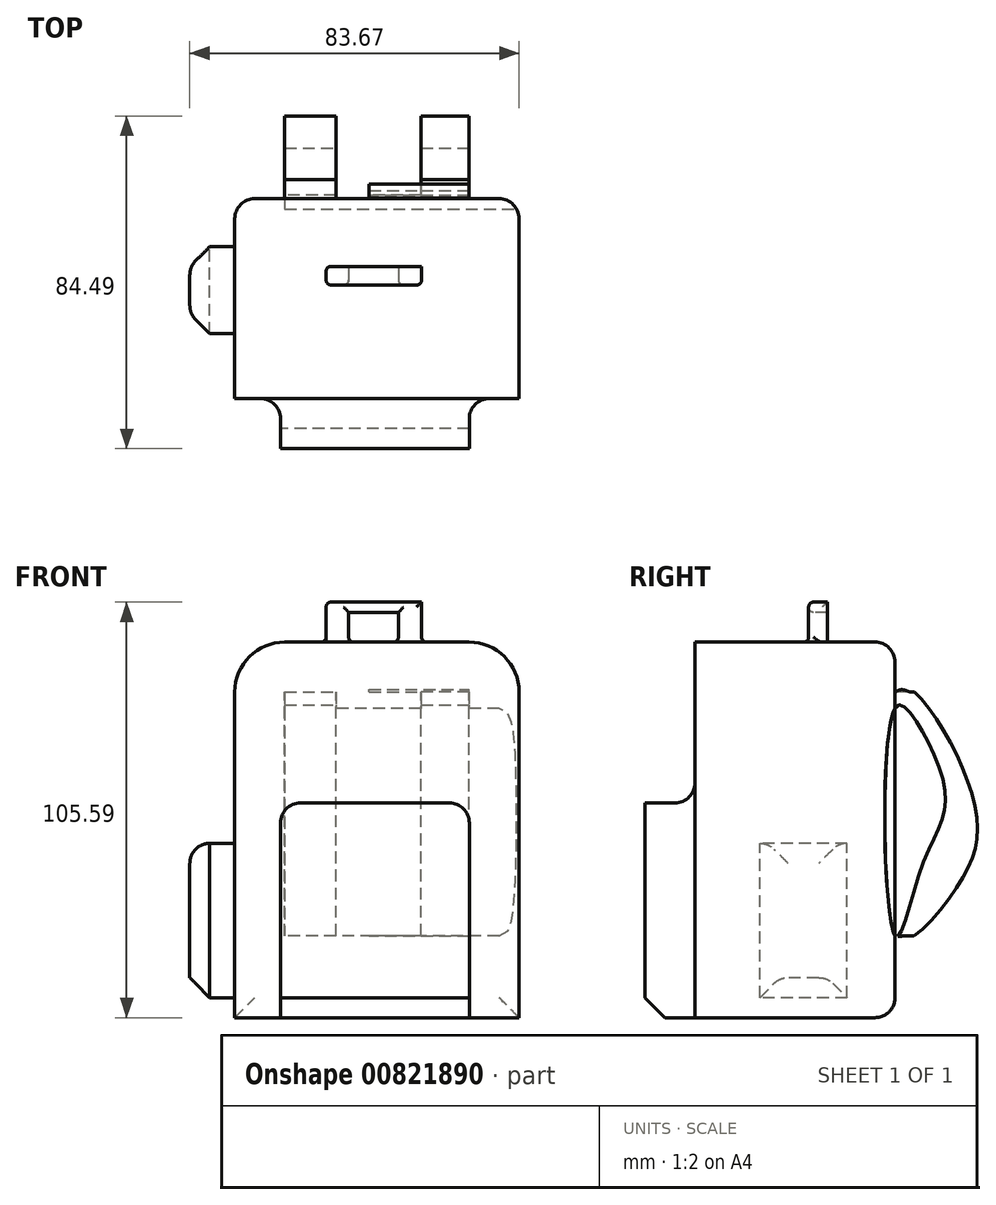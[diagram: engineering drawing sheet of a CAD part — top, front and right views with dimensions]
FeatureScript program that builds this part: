
annotation { "Feature Type Name" : "Feature", "Feature Type Description" : "" }
export const myFeature = defineFeature(function(context is Context, id is Id, definition is map)
    precondition{}
    {
        {
            var Q0;
            Q0=qCreatedBy(makeId("Front.planeOp"),FACE);
            var sketch = newSketch(context, id + "F0", { "sketchPlane" : qUnion([Q0])});
            skLineSegment(sketch, "E0.bottom", {"start": v(-29.99, 56.61) * mm, "end": v(42.25, 56.61) * mm});
            skLineSegment(sketch, "E0.top", {"start": v(-29.99, -38.82) * mm, "end": v(42.25, -38.82) * mm});
            skLineSegment(sketch, "E0.left", {"start": v(-29.99, 56.61) * mm, "end": v(-29.99, -38.82) * mm});
            skLineSegment(sketch, "E0.right", {"start": v(42.25, 56.61) * mm, "end": v(42.25, -38.82) * mm});
            skSolve(sketch);
        }
        {
            var Q0;
            Q0 = qSketchRegion(id + "F0", true);
            extrude(context, id + "F1", {"entities" : qUnion([Q0]), "depth" : 63.5 * mm, "offsetDistance" : 25.4 * mm});
        }
        {
            var Q0;
            Q0=makeQuery(id+"F1.opExtrude","CAP_FACE",FACE,{"disambiguationData":[OSD([sQuery(id+"F0.wireOp",EDGE,"E0.bottom"),sQuery(id+"F0.wireOp",EDGE,"E0.top"),sQuery(id+"F0.wireOp",EDGE,"E0.left"),sQuery(id+"F0.wireOp",EDGE,"E0.right")])],"isStart":false});
            var sketch = newSketch(context, id + "F2", { "sketchPlane" : qUnion([Q0])});
            skLineSegment(sketch, "E1.bottom", {"start": v(-18.39, -38.82) * mm, "end": v(29.6, -38.82) * mm});
            skLineSegment(sketch, "E1.top", {"start": v(-18.39, 15.75) * mm, "end": v(29.6, 15.75) * mm});
            skLineSegment(sketch, "E1.left", {"start": v(-18.39, -38.82) * mm, "end": v(-18.39, 15.75) * mm});
            skLineSegment(sketch, "E1.right", {"start": v(29.6, -38.82) * mm, "end": v(29.6, 15.75) * mm});
            skSolve(sketch);
        }
        {
            var Q0;
            Q0=makeQuery(id+"F2.imprint","IMPRINT",FACE,{"disambiguationData":[TD([[makeQuery(id+"F2.imprint","IMPRINT",EDGE,{"derivedFrom":sQuery(id+"F2.wireOp",EDGE,"E1.top")}),1.0]])]});
            extrude(context, id + "F3", {"entities" : qUnion([Q0]), "operationType" : NewBodyOperationType.REMOVE, "oppositeDirection" : true, "depth" : 12.7 * mm, "offsetDistance" : 25.4 * mm});
        }
        {
            var Q0;
            Q0=makeQuery(id+"F3.boolean.opBoolean","COPY",EDGE,{"derivedFrom":makeQuery(id+"F3.opExtrude","CAP_EDGE",EDGE,{"disambiguationData":[OSD([sQuery(id+"F2.wireOp",EDGE,"E1.left")])],"isStart":true})});
            var Q1;
            Q1=makeQuery(id+"F3.boolean.opBoolean","COPY",EDGE,{"derivedFrom":makeQuery(id+"F3.opExtrude","CAP_EDGE",EDGE,{"disambiguationData":[OSD([sQuery(id+"F2.wireOp",EDGE,"E1.top")])],"isStart":true})});
            var Q2;
            Q2=makeQuery(id+"F3.boolean.opBoolean","COPY",EDGE,{"derivedFrom":makeQuery(id+"F3.opExtrude","CAP_EDGE",EDGE,{"disambiguationData":[OSD([sQuery(id+"F2.wireOp",EDGE,"E1.top")])],"isStart":false})});
            var Q3;
            Q3=makeQuery(id+"F3.boolean.opBoolean","COPY",EDGE,{"derivedFrom":makeQuery(id+"F3.opExtrude","CAP_EDGE",EDGE,{"disambiguationData":[OSD([sQuery(id+"F2.wireOp",EDGE,"E1.left")])],"isStart":false})});
            var Q4;
            Q4=makeQuery(id+"F3.boolean.opBoolean","COPY",EDGE,{"derivedFrom":makeQuery(id+"F3.opExtrude","CAP_EDGE",EDGE,{"disambiguationData":[OSD([sQuery(id+"F2.wireOp",EDGE,"E1.right")])],"isStart":false})});
            var Q5;
            Q5=makeQuery(id+"F3.boolean.opBoolean","COPY",EDGE,{"derivedFrom":makeQuery(id+"F3.opExtrude","CAP_EDGE",EDGE,{"disambiguationData":[OSD([sQuery(id+"F2.wireOp",EDGE,"E1.right")])],"isStart":true})});
            var Q6;
            Q6=makeQuery(id+"F3.boolean.opBoolean","COPY",EDGE,{"derivedFrom":makeQuery(id+"F3.opExtrude","SWEPT_EDGE",EDGE,{"disambiguationData":[OSD([sQuery(id+"F2.wireOp",EDGE,"E1.top"),sQuery(id+"F2.wireOp",EDGE,"E1.right")])]})});
            var Q7;
            Q7=makeQuery(id+"F3.boolean.opBoolean","COPY",EDGE,{"derivedFrom":makeQuery(id+"F3.opExtrude","SWEPT_EDGE",EDGE,{"disambiguationData":[OSD([sQuery(id+"F2.wireOp",EDGE,"E1.top"),sQuery(id+"F2.wireOp",EDGE,"E1.left")])]})});
            fillet(context, id + "F4", {"entities" : qUnion([Q0, Q1, Q2, Q3, Q4, Q5, Q6, Q7]), "radius" : 5.08 * mm, "tangentPropagation" : true, "allowEdgeOverflow" : false});
        }
        {
            var Q0;
            Q0=makeQuery(id+"F3.boolean.opBoolean","COPY",EDGE,{"derivedFrom":makeQuery(id+"F3.opExtrude","CAP_EDGE",EDGE,{"disambiguationData":[OSD([sQuery(id+"F0.wireOp",EDGE,"E0.bottom")])],"isStart":false})});
            var Q1;
            Q1=makeQuery(id+"F3.boolean.opBoolean","COPY",EDGE,{"derivedFrom":makeQuery(id+"F3.opExtrude","CAP_EDGE",EDGE,{"disambiguationData":[OSD([sQuery(id+"F0.wireOp",EDGE,"E0.right")])],"isStart":false})});
            var Q2;
            Q2=makeQuery(id+"F3.boolean.opBoolean","COPY",EDGE,{"derivedFrom":makeQuery(id+"F3.opExtrude","CAP_EDGE",EDGE,{"disambiguationData":[OSD([sQuery(id+"F0.wireOp",EDGE,"E0.left")])],"isStart":false})});
            var Q3;
            Q3=makeQuery(id+"F1.opExtrude","SWEPT_EDGE",EDGE,{"disambiguationData":[OSD([sQuery(id+"F0.wireOp",EDGE,"E0.bottom"),sQuery(id+"F0.wireOp",EDGE,"E0.right")])]});
            var Q4;
            Q4=makeQuery(id+"F1.opExtrude","SWEPT_EDGE",EDGE,{"disambiguationData":[OSD([sQuery(id+"F0.wireOp",EDGE,"E0.bottom"),sQuery(id+"F0.wireOp",EDGE,"E0.left")])]});
            fillet(context, id + "F5", {"entities" : qUnion([Q0, Q1, Q2, Q3, Q4]), "radius" : 12.7 * mm, "tangentPropagation" : true, "allowEdgeOverflow" : false});
        }
        {
            var Q0;
            Q0=makeQuery(id+"F1.opExtrude","CAP_EDGE",EDGE,{"disambiguationData":[OSD([sQuery(id+"F0.wireOp",EDGE,"E0.top")])],"isStart":false});
            chamfer(context, id + "F6", {"entities" : qUnion([Q0]), "width" : 5.08 * mm, "tangentPropagation" : true});
        }
        {
            var Q0;
            Q0=makeQuery(id+"F1.opExtrude","SWEPT_FACE",FACE,{"disambiguationData":[OSD([sQuery(id+"F0.wireOp",EDGE,"E0.top")])]});
            var sketch = newSketch(context, id + "F7", { "sketchPlane" : qUnion([Q0])});
            skCircle(sketch, "E2", {"center": v(-11.8, 31.57) * mm, "radius": 11.04 * mm});
            skCircle(sketch, "E3", {"center": v(24.06, 31.3) * mm, "radius": 11.04 * mm});
            skSolve(sketch);
        }
        {
            var Q0;
            Q0=sQuery(id+"F7.wireOp",EDGE,"E2");
            var Q1;
            Q1=sQuery(id+"F7.wireOp",EDGE,"E3");
            extrude(context, id + "F8", {"bodyType" : ToolBodyType.SURFACE, "surfaceEntities" : qUnion([Q0, Q1]), "depth" : 2.54 * mm, "offsetDistance" : 25.4 * mm});
        }
        {
            var Q0;
            Q0=makeQuery(id+"F1.opExtrude","SWEPT_FACE",FACE,{"disambiguationData":[OSD([sQuery(id+"F0.wireOp",EDGE,"E0.left")])]});
            var sketch = newSketch(context, id + "F9", { "sketchPlane" : qUnion([Q0])});
            skLineSegment(sketch, "E4.bottom", {"start": v(12.2, -33.74) * mm, "end": v(34.34, -33.74) * mm});
            skLineSegment(sketch, "E4.top", {"start": v(12.2, 5.47) * mm, "end": v(34.34, 5.47) * mm});
            skLineSegment(sketch, "E4.left", {"start": v(12.2, -33.74) * mm, "end": v(12.2, 5.47) * mm});
            skLineSegment(sketch, "E4.right", {"start": v(34.34, -33.74) * mm, "end": v(34.34, 5.47) * mm});
            skSolve(sketch);
        }
        {
            var Q0;
            Q0=makeQuery(id+"F9.imprint","IMPRINT",FACE,{"disambiguationData":[TD([[makeQuery(id+"F9.imprint","IMPRINT",EDGE,{"derivedFrom":sQuery(id+"F9.wireOp",EDGE,"E4.bottom")}),1.0]])]});
            extrude(context, id + "F10", {"entities" : qUnion([Q0]), "operationType" : NewBodyOperationType.ADD, "depth" : 11.43 * mm, "offsetDistance" : 25.4 * mm});
        }
        {
            var Q0;
            Q0=makeQuery(id+"F10.opExtrude","CAP_EDGE",EDGE,{"disambiguationData":[OSD([sQuery(id+"F9.wireOp",EDGE,"E4.right")])],"isStart":false});
            var Q1;
            Q1=makeQuery(id+"F10.opExtrude","CAP_EDGE",EDGE,{"disambiguationData":[OSD([sQuery(id+"F9.wireOp",EDGE,"E4.left")])],"isStart":false});
            var Q2;
            Q2=makeQuery(id+"F10.opExtrude","CAP_EDGE",EDGE,{"disambiguationData":[OSD([sQuery(id+"F9.wireOp",EDGE,"E4.bottom")])],"isStart":false});
            var Q3;
            Q3=makeQuery(id+"F10.opExtrude","CAP_EDGE",EDGE,{"disambiguationData":[OSD([sQuery(id+"F9.wireOp",EDGE,"E4.top")])],"isStart":true});
            chamfer(context, id + "F11", {"entities" : qUnion([Q0, Q1, Q2, Q3]), "width" : 5.08 * mm, "tangentPropagation" : true});
        }
        {
            var Q0;
            Q0=makeQuery(id+"F10.opExtrude","CAP_EDGE",EDGE,{"disambiguationData":[OSD([sQuery(id+"F9.wireOp",EDGE,"E4.right")])],"isStart":true});
            var Q1;
            Q1=makeQuery(id+"F10.opExtrude","CAP_EDGE",EDGE,{"disambiguationData":[OSD([sQuery(id+"F9.wireOp",EDGE,"E4.left")])],"isStart":true});
            var Q2;
            {var subQ0=sQuery(id+"F9.wireOp",EDGE,"E4.left");Q2=makeQuery(id+"F11.opChamfer","BLEND_EDGE",EDGE,{"blendedFrom":[makeQuery(id+"F10.opExtrude","CAP_EDGE",EDGE,{"disambiguationData":[OSD([subQ0])],"isStart":false}),makeQuery(id+"F10.opExtrude","CAP_FACE",FACE,{"disambiguationData":[OSD([sQuery(id+"F9.wireOp",EDGE,"E4.bottom"),sQuery(id+"F9.wireOp",EDGE,"E4.top"),subQ0,sQuery(id+"F9.wireOp",EDGE,"E4.right")])],"isStart":false})],"blendedInto":[makeQuery(id+"F10.opExtrude","CAP_FACE",FACE,{"disambiguationData":[OSD([sQuery(id+"F9.wireOp",EDGE,"E4.bottom"),sQuery(id+"F9.wireOp",EDGE,"E4.top"),subQ0,sQuery(id+"F9.wireOp",EDGE,"E4.right")])],"isStart":false})]});}
            var Q3;
            {var subQ0=sQuery(id+"F9.wireOp",EDGE,"E4.right");Q3=makeQuery(id+"F11.opChamfer","BLEND_EDGE",EDGE,{"blendedFrom":[makeQuery(id+"F10.opExtrude","CAP_EDGE",EDGE,{"disambiguationData":[OSD([subQ0])],"isStart":false}),makeQuery(id+"F10.opExtrude","CAP_FACE",FACE,{"disambiguationData":[OSD([sQuery(id+"F9.wireOp",EDGE,"E4.bottom"),sQuery(id+"F9.wireOp",EDGE,"E4.top"),sQuery(id+"F9.wireOp",EDGE,"E4.left"),subQ0])],"isStart":false})],"blendedInto":[makeQuery(id+"F10.opExtrude","CAP_FACE",FACE,{"disambiguationData":[OSD([sQuery(id+"F9.wireOp",EDGE,"E4.bottom"),sQuery(id+"F9.wireOp",EDGE,"E4.top"),sQuery(id+"F9.wireOp",EDGE,"E4.left"),subQ0])],"isStart":false})]});}
            var Q4;
            Q4=makeQuery(id+"F10.opExtrude","CAP_EDGE",EDGE,{"disambiguationData":[OSD([sQuery(id+"F9.wireOp",EDGE,"E4.top")])],"isStart":false});
            fillet(context, id + "F12", {"entities" : qUnion([Q0, Q1, Q2, Q3, Q4]), "radius" : 5.08 * mm, "tangentPropagation" : true, "allowEdgeOverflow" : false});
        }
        {
            var Q0;
            Q0=makeQuery(id+"F1.opExtrude","SWEPT_FACE",FACE,{"disambiguationData":[OSD([sQuery(id+"F0.wireOp",EDGE,"E0.bottom")])]});
            var sketch = newSketch(context, id + "F13", { "sketchPlane" : qUnion([Q0])});
            skLineSegment(sketch, "E5.bottom", {"start": v(-6.79, -17.2) * mm, "end": v(17.47, -17.2) * mm});
            skLineSegment(sketch, "E5.top", {"start": v(-6.79, -21.95) * mm, "end": v(17.47, -21.95) * mm});
            skLineSegment(sketch, "E5.left", {"start": v(-6.79, -17.2) * mm, "end": v(-6.79, -21.95) * mm});
            skLineSegment(sketch, "E5.right", {"start": v(17.47, -17.2) * mm, "end": v(17.47, -21.95) * mm});
            skSolve(sketch);
        }
        {
            var Q0;
            Q0 = qSketchRegion(id + "F13", true);
            extrude(context, id + "F14", {"entities" : qUnion([Q0]), "operationType" : NewBodyOperationType.ADD, "depth" : 10.16 * mm, "offsetDistance" : 25.4 * mm});
        }
        {
            var Q0;
            Q0=makeQuery(id+"F14.opExtrude","SWEPT_FACE",FACE,{"disambiguationData":[OSD([sQuery(id+"F13.wireOp",EDGE,"E5.top")])]});
            var sketch = newSketch(context, id + "F15", { "sketchPlane" : qUnion([Q0])});
            skLineSegment(sketch, "E6.bottom", {"start": v(-1.06, 56.61) * mm, "end": v(11.59, 56.61) * mm});
            skLineSegment(sketch, "E6.top", {"start": v(-1.06, 64.17) * mm, "end": v(11.59, 64.17) * mm});
            skLineSegment(sketch, "E6.left", {"start": v(-1.06, 56.61) * mm, "end": v(-1.06, 64.17) * mm});
            skLineSegment(sketch, "E6.right", {"start": v(11.59, 56.61) * mm, "end": v(11.59, 64.17) * mm});
            skSolve(sketch);
        }
        {
            var Q0;
            Q0 = qSketchRegion(id + "F15", true);
            extrude(context, id + "F16", {"entities" : qUnion([Q0]), "operationType" : NewBodyOperationType.REMOVE, "endBound" : BoundingType.THROUGH_ALL, "oppositeDirection" : true, "depth" : 25.4 * mm, "offsetDistance" : 25.4 * mm});
        }
        {
            var Q0;
            Q0=makeQuery(id+"F14.opExtrude","SWEPT_EDGE",EDGE,{"disambiguationData":[OSD([sQuery(id+"F13.wireOp",EDGE,"E5.top"),sQuery(id+"F13.wireOp",EDGE,"E5.left")])]});
            var Q1;
            Q1=makeQuery(id+"F14.opExtrude","SWEPT_EDGE",EDGE,{"disambiguationData":[OSD([sQuery(id+"F13.wireOp",EDGE,"E5.bottom"),sQuery(id+"F13.wireOp",EDGE,"E5.left")])]});
            var Q2;
            Q2=makeQuery(id+"F14.opExtrude","CAP_EDGE",EDGE,{"disambiguationData":[OSD([sQuery(id+"F13.wireOp",EDGE,"E5.left")])],"isStart":false});
            var Q3;
            Q3=makeQuery(id+"F14.opExtrude","CAP_EDGE",EDGE,{"disambiguationData":[OSD([sQuery(id+"F13.wireOp",EDGE,"E5.top")])],"isStart":false});
            var Q4;
            Q4=makeQuery(id+"F14.opExtrude","SWEPT_FACE",FACE,{"disambiguationData":[OSD([sQuery(id+"F13.wireOp",EDGE,"E5.top")])]});
            fillet(context, id + "F17", {"entities" : qUnion([Q0, Q1, Q2, Q3, Q4]), "radius" : 1.27 * mm, "tangentPropagation" : true, "allowEdgeOverflow" : false});
        }
        {
            var Q0;
            Q0=makeQuery(id+"F1.opExtrude","CAP_FACE",FACE,{"disambiguationData":[OSD([sQuery(id+"F0.wireOp",EDGE,"E0.bottom"),sQuery(id+"F0.wireOp",EDGE,"E0.top"),sQuery(id+"F0.wireOp",EDGE,"E0.left"),sQuery(id+"F0.wireOp",EDGE,"E0.right")])],"isStart":true});
            fillet(context, id + "F18", {"entities" : qUnion([Q0]), "radius" : 5.08 * mm, "tangentPropagation" : true, "allowEdgeOverflow" : false});
        }
        {
            var Q0;
            Q0=makeQuery(id+"F1.opExtrude","CAP_FACE",FACE,{"disambiguationData":[OSD([sQuery(id+"F0.wireOp",EDGE,"E0.bottom"),sQuery(id+"F0.wireOp",EDGE,"E0.top"),sQuery(id+"F0.wireOp",EDGE,"E0.left"),sQuery(id+"F0.wireOp",EDGE,"E0.right")])],"isStart":true});
            var sketch = newSketch(context, id + "F19", { "sketchPlane" : qUnion([Q0])});
            skLineSegment(sketch, "E7.bottom", {"start": v(-29.55, 43.91) * mm, "end": v(-17.33, 43.91) * mm});
            skLineSegment(sketch, "E7.top", {"start": v(-29.55, -18) * mm, "end": v(-17.33, -18) * mm});
            skLineSegment(sketch, "E7.left", {"start": v(-29.55, 43.91) * mm, "end": v(-29.55, -18) * mm});
            skLineSegment(sketch, "E7.right", {"start": v(-17.33, 43.91) * mm, "end": v(-17.33, -18) * mm});
            skLineSegment(sketch, "E8.bottom", {"start": v(17.29, 43.91) * mm, "end": v(4.28, 43.91) * mm});
            skLineSegment(sketch, "E8.top", {"start": v(17.29, -18) * mm, "end": v(4.28, -18) * mm});
            skLineSegment(sketch, "E8.left", {"start": v(17.29, 43.91) * mm, "end": v(17.29, -18) * mm});
            skLineSegment(sketch, "E8.right", {"start": v(4.28, 43.91) * mm, "end": v(4.28, -18) * mm});
            skSolve(sketch);
        }
        {
            var Q0;
            Q0 = qSketchRegion(id + "F19", true);
            extrude(context, id + "F20", {"entities" : qUnion([Q0]), "operationType" : NewBodyOperationType.ADD, "depth" : 25.4 * mm, "offsetDistance" : 25.4 * mm});
        }
        {
            var Q0;
            Q0=makeQuery(id+"F20.opExtrude","SWEPT_FACE",FACE,{"disambiguationData":[OSD([sQuery(id+"F19.wireOp",EDGE,"E7.left")])]});
            var sketch = newSketch(context, id + "F21", { "sketchPlane" : qUnion([Q0])});
            skSolve(sketch);
        }
        {
            var Q0;
            {var subQ0=sQuery(id+"F19.wireOp",EDGE,"E7.left");Q0=makeQuery(id+"F21.imprint","IMPRINT",FACE,{"disambiguationData":[TD([[makeQuery(id+"F21.imprint","IMPRINT",EDGE,{"derivedFrom":makeQuery(id+"F20.opExtrude","CAP_EDGE",EDGE,{"disambiguationData":[OSD([subQ0])],"isStart":false})}),-1.0]])]});}
            var sketch = newSketch(context, id + "F22", { "sketchPlane" : qUnion([Q0])});
            skFitSpline(sketch, "E9", {"points": [v(0, 43.78) * mm, v(11.63, 35.58) * mm, v(19.27, 25.7) * mm, v(21.88, 4.26) * mm, v(8.83, -10.46) * mm, v(0, -17.55) * mm, v(0, 43.78) * mm]});
            skSolve(sketch);
        }
        {
            var Q0;
            {var subQ0=sQuery(id+"F22.wireOp",EDGE,"E9");var subQ1=makeQuery(id+"F21.imprint","IMPRINT",EDGE,{"derivedFrom":makeQuery(id+"F20.opExtrude","SWEPT_EDGE",EDGE,{"disambiguationData":[OSD([sQuery(id+"F19.wireOp",EDGE,"E7.bottom"),sQuery(id+"F19.wireOp",EDGE,"E7.left")])]})});var subQ2=makeQuery(id+"F22.imprint","INTERSECT",VERTEX,{"disambiguationData":[OD(0.0)],"derivedFrom":[subQ1,subQ0]});Q0=makeQuery(id+"F22.imprint","IMPRINT",FACE,{"disambiguationData":[TD([[makeQuery(id+"F22.imprint","IMPRINT",EDGE,{"disambiguationData":[TD([[subQ2,-1.0]])],"derivedFrom":subQ0}),-1.0]])]});}
            var Q1;
            {var subQ0=sQuery(id+"F22.wireOp",EDGE,"E9");var subQ1=makeQuery(id+"F21.imprint","IMPRINT",EDGE,{"derivedFrom":makeQuery(id+"F20.opExtrude","SWEPT_EDGE",EDGE,{"disambiguationData":[OSD([sQuery(id+"F19.wireOp",EDGE,"E7.top"),sQuery(id+"F19.wireOp",EDGE,"E7.left")])]})});var subQ2=makeQuery(id+"F22.imprint","INTERSECT",VERTEX,{"disambiguationData":[OD(0.0)],"derivedFrom":[subQ1,subQ0]});Q1=makeQuery(id+"F22.imprint","IMPRINT",FACE,{"disambiguationData":[TD([[makeQuery(id+"F22.imprint","IMPRINT",EDGE,{"disambiguationData":[TD([[subQ2,-1.0]])],"derivedFrom":subQ0}),-1.0]])]});}
            var Q2;
            {var subQ0=sQuery(id+"F22.wireOp",EDGE,"E9");var subQ1=makeQuery(id+"F21.imprint","IMPRINT",EDGE,{"derivedFrom":makeQuery(id+"F20.opExtrude","CAP_EDGE",EDGE,{"disambiguationData":[OSD([sQuery(id+"F19.wireOp",EDGE,"E7.left")])],"isStart":true})});var subQ2=makeQuery(id+"F22.imprint","INTERSECT",VERTEX,{"disambiguationData":[OD(0.0)],"derivedFrom":[subQ1,subQ0]});Q2=makeQuery(id+"F22.imprint","IMPRINT",FACE,{"disambiguationData":[TD([[makeQuery(id+"F22.imprint","IMPRINT",EDGE,{"disambiguationData":[TD([[subQ2,1.0]])],"derivedFrom":subQ0}),-1.0]])]});}
            extrude(context, id + "F23", {"entities" : qUnion([Q0, Q1, Q2]), "operationType" : NewBodyOperationType.ADD, "oppositeDirection" : true, "depth" : 25.4 * mm, "offsetDistance" : 25.4 * mm});
        }
        {
            var Q0;
            Q0=makeQuery(id+"F20.opExtrude","SWEPT_FACE",FACE,{"disambiguationData":[OSD([sQuery(id+"F19.wireOp",EDGE,"E8.left")])]});
            var sketch = newSketch(context, id + "F24", { "sketchPlane" : qUnion([Q0])});
            skSolve(sketch);
        }
        {
            var Q0;
            {var subQ0=sQuery(id+"F19.wireOp",EDGE,"E8.left");Q0=makeQuery(id+"F24.imprint","IMPRINT",FACE,{"disambiguationData":[TD([[makeQuery(id+"F24.imprint","IMPRINT",EDGE,{"derivedFrom":makeQuery(id+"F20.opExtrude","CAP_EDGE",EDGE,{"disambiguationData":[OSD([subQ0])],"isStart":false})}),1.0]])]});}
            var sketch = newSketch(context, id + "F25", { "sketchPlane" : qUnion([Q0])});
            skFitSpline(sketch, "E10", {"points": [v(0, -17.73) * mm, v(-14.82, -6.93) * mm, v(-20.89, 11.27) * mm, v(-9.35, 38.79) * mm, v(0, 43.82) * mm, v(0, -17.73) * mm]});
            skSolve(sketch);
        }
        {
            var Q0;
            {var subQ1=sQuery(id+"F19.wireOp",EDGE,"E8.left");var subQ6=makeQuery(id+"F24.imprint","IMPRINT",EDGE,{"derivedFrom":makeQuery(id+"F20.opExtrude","CAP_EDGE",EDGE,{"disambiguationData":[OSD([subQ1])],"isStart":false})});Q0=makeQuery(id+"F25.imprint","IMPRINT",FACE,{"disambiguationData":[TD([[makeQuery(id+"F25.imprint","IMPRINT",EDGE,{"derivedFrom":subQ6}),1.0]])]});}
            extrude(context, id + "F26", {"entities" : qUnion([Q0]), "operationType" : NewBodyOperationType.REMOVE, "endBound" : BoundingType.THROUGH_ALL, "oppositeDirection" : true, "depth" : 25.4 * mm, "offsetDistance" : 25.4 * mm});
        }
        {
            var Q0;
            Q0=makeQuery(id+"F20.opExtrude","SWEPT_FACE",FACE,{"disambiguationData":[OSD([sQuery(id+"F19.wireOp",EDGE,"E8.left")])]});
            var sketch = newSketch(context, id + "F27", { "sketchPlane" : qUnion([Q0])});
            skFitSpline(sketch, "E11", {"points": [v(0, -18) * mm, v(-6.99, 0) * mm, v(-12.85, 17.1) * mm, v(-4.47, 37.77) * mm, v(0, 39.73) * mm, v(0, -18) * mm]});
            skSolve(sketch);
        }
        {
            var Q0;
            Q0 = qSketchRegion(id + "F27", true);
            extrude(context, id + "F28", {"entities" : qUnion([Q0]), "operationType" : NewBodyOperationType.REMOVE, "endBound" : BoundingType.THROUGH_ALL, "oppositeDirection" : true, "depth" : 25.4 * mm, "offsetDistance" : 25.4 * mm});
        }
    });
